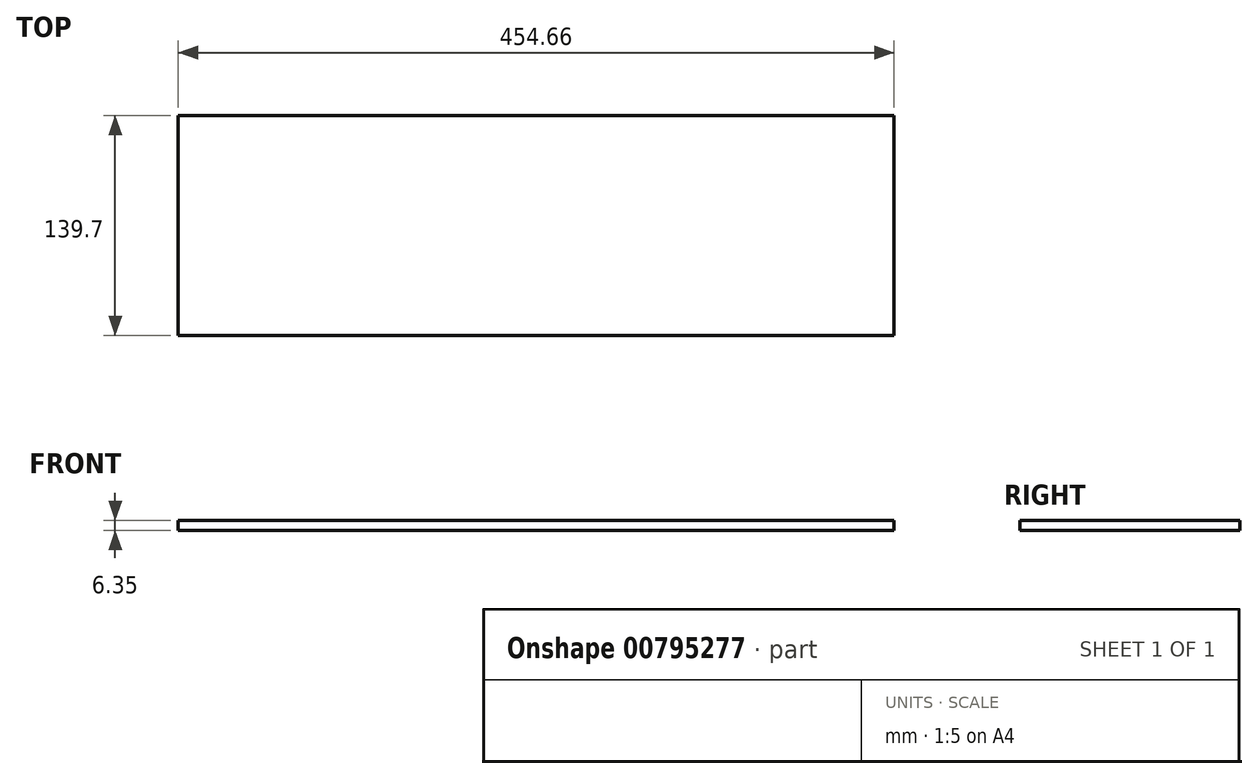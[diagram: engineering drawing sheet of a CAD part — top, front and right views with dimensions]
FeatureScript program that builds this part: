
annotation { "Feature Type Name" : "Feature", "Feature Type Description" : "" }
export const myFeature = defineFeature(function(context is Context, id is Id, definition is map)
    precondition{}
    {
        {
            var Q0;
            Q0=qCreatedBy(makeId("Top.planeOp"),FACE);
            var sketch = newSketch(context, id + "F0", { "sketchPlane" : qUnion([Q0])});
            skLineSegment(sketch, "E0.bottom", {"start": v(227.33, -69.85) * mm, "end": v(-227.33, -69.85) * mm});
            skLineSegment(sketch, "E0.top", {"start": v(227.33, 69.85) * mm, "end": v(-227.33, 69.85) * mm});
            skLineSegment(sketch, "E0.left", {"start": v(227.33, -69.85) * mm, "end": v(227.33, 69.85) * mm});
            skLineSegment(sketch, "E0.right", {"start": v(-227.33, -69.85) * mm, "end": v(-227.33, 69.85) * mm});
            skPoint(sketch, "E0.middle", {"position": v(0, 0) * mm});
            skSolve(sketch);
        }
        {
            var Q0;
            Q0=makeQuery(id+"F0.imprint","IMPRINT",FACE,{"disambiguationData":[TD([[makeQuery(id+"F0.imprint","IMPRINT",EDGE,{"derivedFrom":sQuery(id+"F0.wireOp",EDGE,"E0.bottom")}),-1.0]])]});
            extrude(context, id + "F1", {"entities" : qUnion([Q0]), "depth" : 6.35 * mm, "offsetDistance" : 25.4 * mm});
        }
    });
